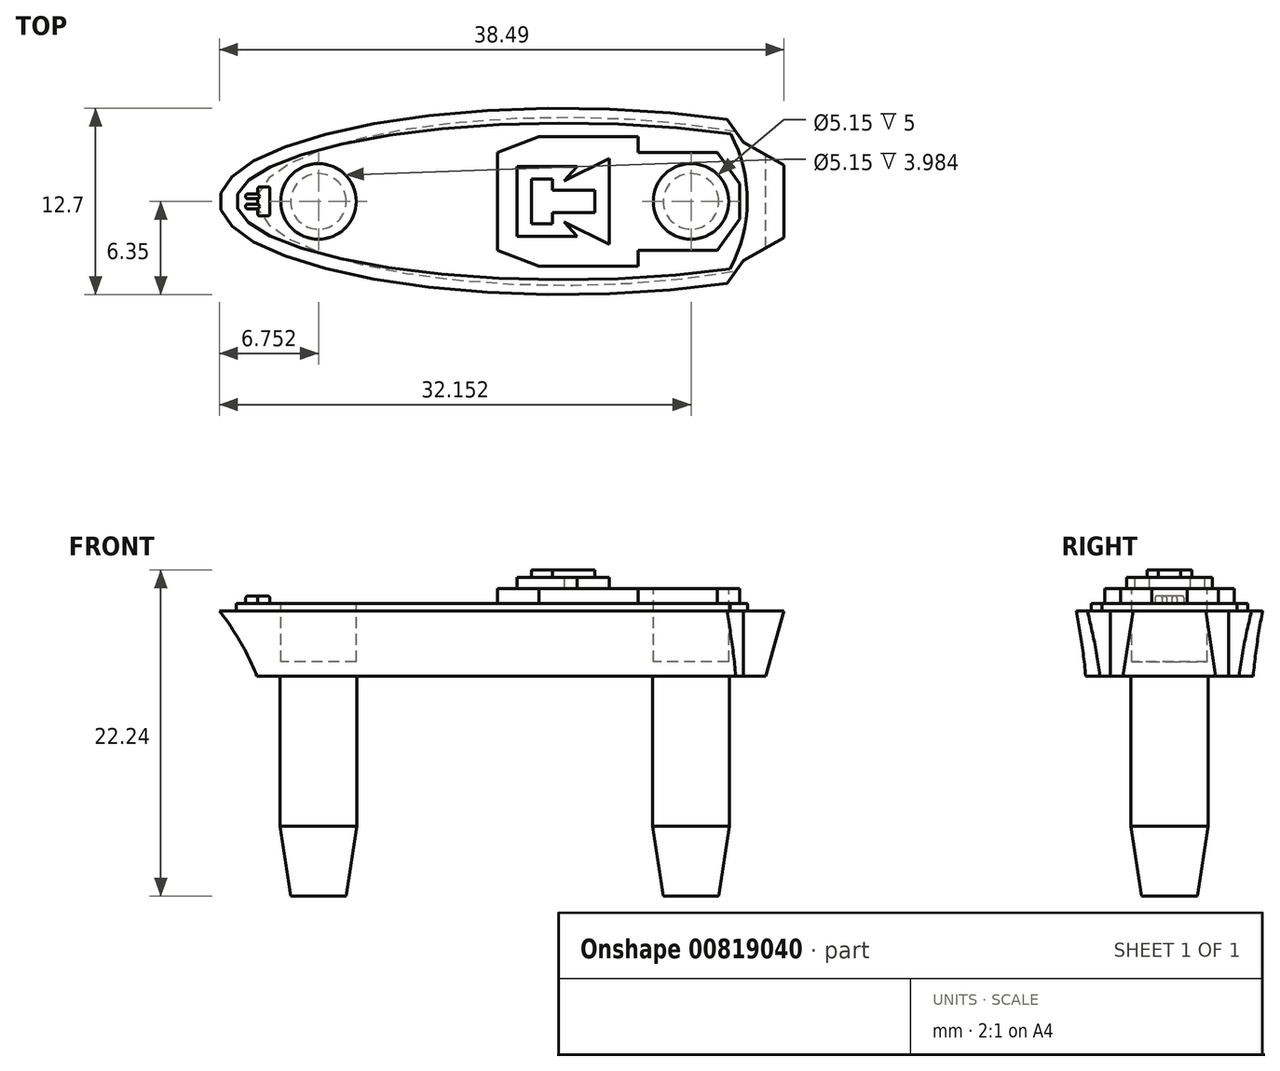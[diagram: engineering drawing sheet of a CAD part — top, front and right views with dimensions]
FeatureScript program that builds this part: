
annotation { "Feature Type Name" : "Feature", "Feature Type Description" : "" }
export const myFeature = defineFeature(function(context is Context, id is Id, definition is map)
    precondition{}
    {
        {
            var Q0;
            Q0=qCreatedBy(makeId("Top.planeOp"),FACE);
            var sketch = newSketch(context, id + "F0", { "sketchPlane" : qUnion([Q0])});
            skEllipse(sketch, "E0", {"center": v(0, 0) * mm, "majorRadius": 20.96 * mm, "minorRadius": 5.72 * mm, "majorAxis": v(1, 0)});
            skSolve(sketch);
        }
        {
            var Q0;
            Q0=qCreatedBy(makeId("Top.planeOp"),FACE);
            cPlane(context, id + "F1", {"entities" : qUnion([Q0]), "cplaneType" : CPlaneType.OFFSET, "offset" : 4.44 * mm, "width" : 152.4 * mm, "height" : 152.4 * mm});
        }
        {
            var Q0;
            Q0=qCreatedBy(id+"F1.planeOp",FACE);
            var sketch = newSketch(context, id + "F2", { "sketchPlane" : qUnion([Q0])});
            skEllipse(sketch, "E1", {"center": v(0, 0) * mm, "majorRadius": 23.5 * mm, "minorRadius": 6.35 * mm, "majorAxis": v(1, 0)});
            skPoint(sketch, "E2", {"position": v(23.5, 0) * mm});
            skSolve(sketch);
        }
        {
            var Q0;
            Q0=makeQuery(id+"F0.imprint","IMPRINT",FACE,{"disambiguationData":[TD([[makeQuery(id+"F0.imprint","IMPRINT",EDGE,{"derivedFrom":sQuery(id+"F0.wireOp",EDGE,"E0")}),1.0]])]});
            var Q1;
            Q1=makeQuery(id+"F2.imprint","IMPRINT",FACE,{"disambiguationData":[TD([[makeQuery(id+"F2.imprint","IMPRINT",EDGE,{"derivedFrom":sQuery(id+"F2.wireOp",EDGE,"E1")}),1.0]])]});
            loft(context, id + "F3", {"sheetProfilesArray" : [{ "sheetProfileEntities" : qUnion([Q0]) }, { "sheetProfileEntities" : qUnion([Q1]) }]});
        }
        {
            var Q0;
            Q0=qCreatedBy(makeId("Front.planeOp"),FACE);
            var sketch = newSketch(context, id + "F4", { "sketchPlane" : qUnion([Q0])});
            skLineSegment(sketch, "E3", {"start": v(12.95, -2.92) * mm, "end": v(15.07, 4.71) * mm});
            skPoint(sketch, "E4", {"position": v(14.6, 3.05) * mm});
            skPoint(sketch, "E5", {"position": v(13.76, 0) * mm});
            skPoint(sketch, "E6", {"position": v(-23.5, 3.05) * mm});
            skSolve(sketch);
        }
        {
            var Q0;
            Q0=sQuery(id+"F4.wireOp",EDGE,"E3");
            cPlane(context, id + "F5", {"entities" : qUnion([Q0]), "cplaneType" : CPlaneType.LINE_ANGLE, "offset" : 25.4 * mm, "angle" : 0 * degree, "width" : 152.4 * mm, "height" : 152.4 * mm});
        }
        {
            var Q0;
            Q0=qCreatedBy(id+"F5.planeOp",FACE);
            var sketch = newSketch(context, id + "F6", { "sketchPlane" : qUnion([Q0])});
            skLineSegment(sketch, "E7.bottom", {"start": v(-4.95, 12.51) * mm, "end": v(5, 12.51) * mm});
            skLineSegment(sketch, "E7.top", {"start": v(-4.95, 0.69) * mm, "end": v(5, 0.69) * mm});
            skLineSegment(sketch, "E7.left", {"start": v(-4.95, 12.51) * mm, "end": v(-4.95, 0.69) * mm});
            skLineSegment(sketch, "E7.right", {"start": v(5, 12.51) * mm, "end": v(5, 0.69) * mm});
            skSolve(sketch);
        }
        {
            var Q0;
            Q0=makeQuery(id+"F6.imprint","IMPRINT",FACE,{"disambiguationData":[TD([[makeQuery(id+"F6.imprint","IMPRINT",EDGE,{"derivedFrom":sQuery(id+"F6.wireOp",EDGE,"E7.bottom")}),-1.0]])]});
            extrude(context, id + "F7", {"entities" : qUnion([Q0]), "operationType" : NewBodyOperationType.REMOVE, "oppositeDirection" : true, "depth" : -76.2 * mm, "offsetDistance" : 25.4 * mm});
        }
        {
            var Q0;
            Q0=makeQuery(id+"F3.opLoft","CAP_FACE",FACE,{"disambiguationData":[OSD([makeQuery(id+"F2.imprint","IMPRINT",FACE,{"disambiguationData":[TD([[makeQuery(id+"F2.imprint","IMPRINT",EDGE,{"derivedFrom":sQuery(id+"F2.wireOp",EDGE,"E1")}),1.0]])]})])],"isStart":true});
            var sketch = newSketch(context, id + "F8", { "sketchPlane" : qUnion([Q0])});
            skLineSegment(sketch, "E8", {"start": v(-24.83, 0) * mm, "end": v(22.16, 0) * mm, "construction": true});
            skLineSegment(sketch, "E9", {"start": v(11.1, -5.6) * mm, "end": v(12.2, -4.02) * mm});
            skLineSegment(sketch, "E10", {"start": v(12.2, -4.02) * mm, "end": v(15, -2.47) * mm});
            skLineSegment(sketch, "E11", {"start": v(11.1, -5.6) * mm, "end": v(12.84, -9.26) * mm});
            skLineSegment(sketch, "E12", {"start": v(12.84, -9.26) * mm, "end": v(16.72, -4.38) * mm});
            skLineSegment(sketch, "E13", {"start": v(16.72, -4.38) * mm, "end": v(15, -2.47) * mm});
            skLineSegment(sketch, "E14.MirrorCS", {"start": v(11.1, 5.6) * mm, "end": v(12.2, 4.02) * mm});
            skLineSegment(sketch, "E15.MirrorCS", {"start": v(12.2, 4.02) * mm, "end": v(15, 2.47) * mm});
            skLineSegment(sketch, "E16.MirrorCS", {"start": v(11.1, 5.6) * mm, "end": v(12.84, 9.26) * mm});
            skLineSegment(sketch, "E17.MirrorCS", {"start": v(12.84, 9.26) * mm, "end": v(16.72, 4.38) * mm});
            skLineSegment(sketch, "E18.MirrorCS", {"start": v(16.72, 4.38) * mm, "end": v(15, 2.47) * mm});
            skSolve(sketch);
        }
        {
            var Q0;
            {var subQ0=sQuery(id+"F8.wireOp",EDGE,"E9");Q0=makeQuery(id+"F8.imprint","IMPRINT",FACE,{"disambiguationData":[TD([[makeQuery(id+"F8.imprint","IMPRINT",EDGE,{"derivedFrom":subQ0}),-1.0]])]});}
            var Q1;
            {var subQ0=sQuery(id+"F8.wireOp",EDGE,"E14.MirrorCS");Q1=makeQuery(id+"F8.imprint","IMPRINT",FACE,{"disambiguationData":[TD([[makeQuery(id+"F8.imprint","IMPRINT",EDGE,{"derivedFrom":subQ0}),1.0]])]});}
            extrude(context, id + "F9", {"entities" : qUnion([Q0, Q1]), "operationType" : NewBodyOperationType.REMOVE, "endBound" : BoundingType.THROUGH_ALL, "oppositeDirection" : true, "depth" : 25.4 * mm, "offsetDistance" : 25.4 * mm});
        }
        {
            var Q0;
            Q0=makeQuery(id+"F3.opLoft","CAP_FACE",FACE,{"disambiguationData":[OSD([makeQuery(id+"F2.imprint","IMPRINT",FACE,{"disambiguationData":[TD([[makeQuery(id+"F2.imprint","IMPRINT",EDGE,{"derivedFrom":sQuery(id+"F2.wireOp",EDGE,"E1")}),1.0]])]})])],"isStart":true});
            var sketch = newSketch(context, id + "F10", { "sketchPlane" : qUnion([Q0])});
            skEllipticalArc(sketch, "E19", {});
            skArc(sketch, "E20", {"start": v(11.31, -4.6) * mm, "mid": v(12.5, 0) * mm, "end": v(11.36, 4.6) * mm});
            skLineSegment(sketch, "E21", {"start": v(0, 0) * mm, "end": v(2.75, 0.04) * mm, "construction": true});
            const initialGuessF10  = {"E19": [0, 0, -1, 0, 0.022352, 0.005334, 4.179158944691912, 2.101455414401311]};
            skSetInitialGuess(sketch, initialGuessF10);
            skSolve(sketch);
        }
        {
            var Q0;
            Q0=makeQuery(id+"F10.imprint","IMPRINT",FACE,{"disambiguationData":[TD([[makeQuery(id+"F10.imprint","IMPRINT",EDGE,{"derivedFrom":sQuery(id+"F10.wireOp",EDGE,"E19")}),1.0]])]});
            extrude(context, id + "F11", {"entities" : qUnion([Q0]), "operationType" : NewBodyOperationType.ADD, "depth" : 0.5 * mm, "offsetDistance" : 25.4 * mm});
        }
        {
            var Q0;
            Q0=makeQuery(id+"F11.opExtrude","CAP_FACE",FACE,{"disambiguationData":[OSD([sQuery(id+"F10.wireOp",EDGE,"E19"),sQuery(id+"F10.wireOp",EDGE,"E20")])],"isStart":false});
            var sketch = newSketch(context, id + "F12", { "sketchPlane" : qUnion([Q0])});
            skLineSegment(sketch, "E22.left", {"start": v(11.95, -1.2) * mm, "end": v(11.95, 1.2) * mm});
            skLineSegment(sketch, "E23.top", {"start": v(5.04, 4.42) * mm, "end": v(-1.7, 4.42) * mm});
            skLineSegment(sketch, "E23.left", {"start": v(5.04, -4.42) * mm, "end": v(5.04, -3.33) * mm});
            skLineSegment(sketch, "E23.right", {"start": v(-4.55, -4.42) * mm, "end": v(-4.55, -4.42) * mm});
            skLineSegment(sketch, "E24.trimOffspring", {"start": v(5.04, 3.33) * mm, "end": v(5.04, 4.42) * mm});
            skLineSegment(sketch, "E25", {"start": v(-9.84, 0) * mm, "end": v(11.02, 0) * mm, "construction": true});
            skLineSegment(sketch, "E26", {"start": v(-4.55, 3.33) * mm, "end": v(-1.7, 4.42) * mm});
            skLineSegment(sketch, "E27.MirrorCS", {"start": v(10.44, 3.33) * mm, "end": v(5.04, 3.33) * mm});
            skLineSegment(sketch, "E28", {"start": v(10.44, 3.33) * mm, "end": v(11.95, 1.2) * mm});
            skPoint(sketch, "E29.orphan", {"position": v(-4.55, 4.42) * mm});
            skLineSegment(sketch, "E30.trimOffspring", {"start": v(11.95, 3.33) * mm, "end": v(11.95, 3.33) * mm});
            skPoint(sketch, "E31.MirrorCS.start.orphan", {"position": v(5.04, 4.42) * mm});
            skPoint(sketch, "E32.MirrorCS.end.orphan", {"position": v(-4.55, -4.42) * mm});
            skPoint(sketch, "E32.MirrorCS.start.orphan", {"position": v(5.04, -4.42) * mm});
            skPoint(sketch, "E33.MirrorCS.end.orphan", {"position": v(5.04, -3.33) * mm});
            skPoint(sketch, "E33.MirrorCS.start.orphan", {"position": v(11.95, -3.33) * mm});
            skLineSegment(sketch, "E34.MirrorCS", {"start": v(-4.55, -3.33) * mm, "end": v(-1.7, -4.42) * mm});
            skLineSegment(sketch, "E35.MirrorCS", {"start": v(10.44, -3.33) * mm, "end": v(11.95, -1.2) * mm});
            skLineSegment(sketch, "E36.MirrorCS", {"start": v(10.44, -3.33) * mm, "end": v(5.04, -3.33) * mm});
            skLineSegment(sketch, "E37.MirrorCS", {"start": v(5.04, -4.42) * mm, "end": v(-1.7, -4.42) * mm});
            skLineSegment(sketch, "E38.trimOffspring", {"start": v(-4.55, -3.33) * mm, "end": v(-4.55, 3.33) * mm});
            skSolve(sketch);
        }
        {
            var Q0;
            Q0=makeQuery(id+"F12.imprint","IMPRINT",FACE,{"disambiguationData":[TD([[makeQuery(id+"F12.imprint","IMPRINT",EDGE,{"derivedFrom":sQuery(id+"F12.wireOp",EDGE,"E22.left")}),1.0]])]});
            extrude(context, id + "F13", {"entities" : qUnion([Q0]), "operationType" : NewBodyOperationType.ADD, "depth" : 1.02 * mm, "offsetDistance" : 25.4 * mm});
        }
        {
            var Q0;
            Q0=makeQuery(id+"F13.opExtrude","CAP_FACE",FACE,{"disambiguationData":[OSD([sQuery(id+"F12.wireOp",EDGE,"E22.left"),sQuery(id+"F12.wireOp",EDGE,"E23.top"),sQuery(id+"F12.wireOp",EDGE,"E23.left"),sQuery(id+"F12.wireOp",EDGE,"E24.trimOffspring"),sQuery(id+"F12.wireOp",EDGE,"E26"),sQuery(id+"F12.wireOp",EDGE,"E27.MirrorCS"),sQuery(id+"F12.wireOp",EDGE,"E28"),sQuery(id+"F12.wireOp",EDGE,"E34.MirrorCS"),sQuery(id+"F12.wireOp",EDGE,"E35.MirrorCS"),sQuery(id+"F12.wireOp",EDGE,"E36.MirrorCS"),sQuery(id+"F12.wireOp",EDGE,"E37.MirrorCS"),sQuery(id+"F12.wireOp",EDGE,"E38.trimOffspring")])],"isStart":false});
            var sketch = newSketch(context, id + "F14", { "sketchPlane" : qUnion([Q0])});
            skLineSegment(sketch, "E39", {"start": v(-16.75, 0) * mm, "end": v(8.65, 0) * mm, "construction": true});
            skCircle(sketch, "E40", {"center": v(-16.75, 0) * mm, "radius": 2.58 * mm});
            skCircle(sketch, "E41", {"center": v(8.65, 0) * mm, "radius": 2.58 * mm});
            skSolve(sketch);
        }
        {
            var Q0;
            Q0=makeQuery(id+"F14.imprint","IMPRINT",FACE,{"disambiguationData":[TD([[makeQuery(id+"F14.imprint","IMPRINT",EDGE,{"derivedFrom":sQuery(id+"F14.wireOp",EDGE,"E41")}),-1.0]])]});
            var sketch = newSketch(context, id + "F15", { "sketchPlane" : qUnion([Q0])});
            skLineSegment(sketch, "E42", {"start": v(3.08, -2.93) * mm, "end": v(3.08, 2.93) * mm});
            skLineSegment(sketch, "E43", {"start": v(3.08, 2.93) * mm, "end": v(0, 1.4) * mm});
            skLineSegment(sketch, "E44", {"start": v(0, -1.4) * mm, "end": v(3.08, -2.93) * mm});
            skLineSegment(sketch, "E45", {"start": v(0, -1.4) * mm, "end": v(0.9, -2.38) * mm});
            skLineSegment(sketch, "E46", {"start": v(0.9, -2.38) * mm, "end": v(-3.2, -2.38) * mm});
            skLineSegment(sketch, "E47", {"start": v(-3.2, -2.38) * mm, "end": v(-3.2, 2.38) * mm});
            skLineSegment(sketch, "E48", {"start": v(-3.2, 2.38) * mm, "end": v(0.9, 2.38) * mm});
            skLineSegment(sketch, "E49", {"start": v(0.9, 2.38) * mm, "end": v(0, 1.4) * mm});
            skLineSegment(sketch, "E50", {"start": v(-3.65, 0) * mm, "end": v(-4.7, 0) * mm, "construction": true});
            skPoint(sketch, "E51.orphan", {"position": v(-2.78, 0) * mm});
            skSolve(sketch);
        }
        {
            var Q0;
            Q0=makeQuery(id+"F15.imprint","IMPRINT",FACE,{"disambiguationData":[TD([[makeQuery(id+"F15.imprint","IMPRINT",EDGE,{"derivedFrom":sQuery(id+"F15.wireOp",EDGE,"E42")}),1.0]])]});
            extrude(context, id + "F16", {"entities" : qUnion([Q0]), "operationType" : NewBodyOperationType.ADD, "depth" : 0.76 * mm, "offsetDistance" : 25.4 * mm});
        }
        {
            var Q0;
            Q0=makeQuery(id+"F16.opExtrude","CAP_FACE",FACE,{"disambiguationData":[OSD([sQuery(id+"F15.wireOp",EDGE,"E42"),sQuery(id+"F15.wireOp",EDGE,"E43"),sQuery(id+"F15.wireOp",EDGE,"E44"),sQuery(id+"F15.wireOp",EDGE,"E45"),sQuery(id+"F15.wireOp",EDGE,"E46"),sQuery(id+"F15.wireOp",EDGE,"E47"),sQuery(id+"F15.wireOp",EDGE,"E48"),sQuery(id+"F15.wireOp",EDGE,"E49")])],"isStart":false});
            var sketch = newSketch(context, id + "F17", { "sketchPlane" : qUnion([Q0])});
            skLineSegment(sketch, "E52.bottom", {"start": v(-2.23, 1.53) * mm, "end": v(-0.8, 1.53) * mm});
            skLineSegment(sketch, "E52.top", {"start": v(-2.23, -1.53) * mm, "end": v(-0.8, -1.53) * mm});
            skLineSegment(sketch, "E52.left", {"start": v(-2.23, 1.53) * mm, "end": v(-2.23, -1.53) * mm});
            skLineSegment(sketch, "E52.right", {"start": v(-0.8, 1.53) * mm, "end": v(-0.8, 0.75) * mm});
            skLineSegment(sketch, "E53.bottom", {"start": v(-0.8, 0.75) * mm, "end": v(2.08, 0.75) * mm});
            skLineSegment(sketch, "E53.top", {"start": v(-0.8, -0.75) * mm, "end": v(2.08, -0.75) * mm});
            skLineSegment(sketch, "E53.right", {"start": v(2.08, 0.75) * mm, "end": v(2.08, -0.75) * mm});
            skLineSegment(sketch, "E54.trimOffspring", {"start": v(-0.8, -0.75) * mm, "end": v(-0.8, -1.53) * mm});
            skLineSegment(sketch, "E55", {"start": v(-6.5, 0) * mm, "end": v(-7.44, 0) * mm, "construction": true});
            skSolve(sketch);
        }
        {
            var Q0;
            Q0=makeQuery(id+"F17.imprint","IMPRINT",FACE,{"disambiguationData":[TD([[makeQuery(id+"F17.imprint","IMPRINT",EDGE,{"derivedFrom":sQuery(id+"F17.wireOp",EDGE,"E52.bottom")}),-1.0]])]});
            extrude(context, id + "F18", {"entities" : qUnion([Q0]), "operationType" : NewBodyOperationType.ADD, "depth" : 0.5 * mm, "offsetDistance" : 25.4 * mm});
        }
        {
            var Q0;
            Q0=makeQuery(id+"F3.opLoft","CAP_FACE",FACE,{"disambiguationData":[OSD([makeQuery(id+"F2.imprint","IMPRINT",FACE,{"disambiguationData":[TD([[makeQuery(id+"F2.imprint","IMPRINT",EDGE,{"derivedFrom":sQuery(id+"F2.wireOp",EDGE,"E1")}),1.0]])]})])],"isStart":true});
            var sketch = newSketch(context, id + "F19", { "sketchPlane" : qUnion([Q0])});
            skLineSegment(sketch, "E56.bottom", {"start": v(-20.19, 1) * mm, "end": v(-20.76, 1) * mm});
            skLineSegment(sketch, "E56.top", {"start": v(-20.19, -1) * mm, "end": v(-20.76, -1) * mm});
            skLineSegment(sketch, "E56.left", {"start": v(-20.06, 0.86) * mm, "end": v(-20.06, -0.86) * mm});
            skLineSegment(sketch, "E56.right", {"start": v(-20.88, 0.86) * mm, "end": v(-20.88, 0.5) * mm});
            skLineSegment(sketch, "E57", {"start": v(-17.48, 0) * mm, "end": v(-18.1, 0) * mm, "construction": true});
            skLineSegment(sketch, "E58.bottom", {"start": v(-20.88, 0.5) * mm, "end": v(-21.7, 0.5) * mm});
            skLineSegment(sketch, "E58.top", {"start": v(-20.88, 0.18) * mm, "end": v(-21.7, 0.18) * mm});
            skLineSegment(sketch, "E58.right", {"start": v(-21.7, 0.5) * mm, "end": v(-21.7, 0.18) * mm});
            skLineSegment(sketch, "E59.MirrorCS", {"start": v(-20.88, -0.18) * mm, "end": v(-21.7, -0.18) * mm});
            skLineSegment(sketch, "E60.MirrorCS", {"start": v(-20.88, -0.5) * mm, "end": v(-21.7, -0.5) * mm});
            skLineSegment(sketch, "E61.MirrorCS", {"start": v(-21.7, -0.5) * mm, "end": v(-21.7, -0.18) * mm});
            skLineSegment(sketch, "E62.trimOffspring", {"start": v(-20.88, 0.18) * mm, "end": v(-20.88, -0.18) * mm});
            skLineSegment(sketch, "E63.trimOffspring", {"start": v(-20.88, -0.5) * mm, "end": v(-20.88, -0.86) * mm});
            skArc(sketch, "E64.filletArc", {"start": v(-18.55, 2.93) * mm, "mid": v(-18.64, 2.9) * mm, "end": v(-18.67, 2.8) * mm, "construction": true});
            skPoint(sketch, "E65.visualSharp", {"position": v(-20.88, 1) * mm});
            skArc(sketch, "E65.filletArc", {"start": v(-20.76, 1) * mm, "mid": v(-20.84, 0.95) * mm, "end": v(-20.88, 0.86) * mm});
            skPoint(sketch, "E66.visualSharp", {"position": v(-20.06, 1) * mm});
            skArc(sketch, "E66.filletArc", {"start": v(-20.06, 0.86) * mm, "mid": v(-20.1, 0.95) * mm, "end": v(-20.19, 1) * mm});
            skPoint(sketch, "E67.visualSharp", {"position": v(-20.06, -1) * mm});
            skArc(sketch, "E67.filletArc", {"start": v(-20.19, -1) * mm, "mid": v(-20.1, -0.95) * mm, "end": v(-20.06, -0.86) * mm});
            skPoint(sketch, "E68.visualSharp", {"position": v(-20.88, -1) * mm});
            skArc(sketch, "E68.filletArc", {"start": v(-20.88, -0.86) * mm, "mid": v(-20.84, -0.95) * mm, "end": v(-20.76, -1) * mm});
            skSolve(sketch);
        }
        {
            var Q0;
            Q0=makeQuery(id+"F19.imprint","IMPRINT",FACE,{"disambiguationData":[TD([[makeQuery(id+"F19.imprint","IMPRINT",EDGE,{"derivedFrom":sQuery(id+"F19.wireOp",EDGE,"E56.bottom")}),1.0]])]});
            extrude(context, id + "F20", {"entities" : qUnion([Q0]), "operationType" : NewBodyOperationType.ADD, "depth" : 0.5 * mm, "offsetDistance" : 25.4 * mm});
        }
        {
            var Q0;
            Q0=makeQuery(id+"F14.imprint","IMPRINT",FACE,{"disambiguationData":[TD([[makeQuery(id+"F14.imprint","IMPRINT",EDGE,{"derivedFrom":sQuery(id+"F14.wireOp",EDGE,"E40")}),1.0]])]});
            var Q1;
            Q1=makeQuery(id+"F14.imprint","IMPRINT",FACE,{"disambiguationData":[TD([[makeQuery(id+"F14.imprint","IMPRINT",EDGE,{"derivedFrom":sQuery(id+"F14.wireOp",EDGE,"E41")}),1.0]])]});
            extrude(context, id + "F21", {"entities" : qUnion([Q0, Q1]), "operationType" : NewBodyOperationType.REMOVE, "oppositeDirection" : true, "depth" : 5 * mm, "offsetDistance" : 25.4 * mm});
        }
        {
            var Q0;
            Q0=makeQuery(id+"F3.opLoft","CAP_FACE",FACE,{"disambiguationData":[OSD([makeQuery(id+"F0.imprint","IMPRINT",FACE,{"disambiguationData":[TD([[makeQuery(id+"F0.imprint","IMPRINT",EDGE,{"derivedFrom":sQuery(id+"F0.wireOp",EDGE,"E0")}),1.0]])]})])],"isStart":true});
            var sketch = newSketch(context, id + "F22", { "sketchPlane" : qUnion([Q0])});
            skLineSegment(sketch, "E69", {"start": v(-16.75, 0) * mm, "end": v(8.65, 0) * mm, "construction": true});
            skCircle(sketch, "E70", {"center": v(-16.75, 0) * mm, "radius": 2.62 * mm});
            skCircle(sketch, "E71", {"center": v(8.65, 0) * mm, "radius": 2.62 * mm});
            skSolve(sketch);
        }
        {
            var Q0;
            Q0=makeQuery(id+"F22.imprint","IMPRINT",FACE,{"disambiguationData":[TD([[makeQuery(id+"F22.imprint","IMPRINT",EDGE,{"derivedFrom":sQuery(id+"F22.wireOp",EDGE,"E70")}),1.0]])]});
            var Q1;
            Q1=makeQuery(id+"F22.imprint","IMPRINT",FACE,{"disambiguationData":[TD([[makeQuery(id+"F22.imprint","IMPRINT",EDGE,{"derivedFrom":sQuery(id+"F22.wireOp",EDGE,"E71")}),1.0]])]});
            extrude(context, id + "F23", {"entities" : qUnion([Q0, Q1]), "operationType" : NewBodyOperationType.ADD, "depth" : 15 * mm, "offsetDistance" : 25.4 * mm});
        }
        {
            var Q0;
            Q0=makeQuery(id+"F23.opExtrude","CAP_EDGE",EDGE,{"disambiguationData":[OSD([sQuery(id+"F22.wireOp",EDGE,"E71")])],"isStart":false});
            var Q1;
            Q1=makeQuery(id+"F23.opExtrude","CAP_EDGE",EDGE,{"disambiguationData":[OSD([sQuery(id+"F22.wireOp",EDGE,"E70")])],"isStart":false});
            chamfer(context, id + "F24", {"entities" : qUnion([Q0, Q1]), "chamferType" : ChamferType.TWO_OFFSETS, "width1" : 0.73 * mm, "oppositeDirection" : false, "width2" : 4.76 * mm, "tangentPropagation" : true});
        }
        {
            var Q0;
            Q0 = qSketchRegion(id + "F19", true);
            extrude(context, id + "F25", {"entities" : qUnion([Q0]), "operationType" : NewBodyOperationType.ADD, "depth" : 1 * mm, "offsetDistance" : 25.4 * mm});
        }
        {
            var Q0;
            Q0=makeQuery(id+"F25.opExtrude","CAP_EDGE",EDGE,{"disambiguationData":[OSD([sQuery(id+"F19.wireOp",EDGE,"E56.left")])],"isStart":false});
            var Q1;
            Q1=makeQuery(id+"F25.opExtrude","CAP_EDGE",EDGE,{"disambiguationData":[OSD([sQuery(id+"F19.wireOp",EDGE,"E60.MirrorCS")])],"isStart":false});
            var Q2;
            Q2=makeQuery(id+"F25.opExtrude","CAP_EDGE",EDGE,{"disambiguationData":[OSD([sQuery(id+"F19.wireOp",EDGE,"E58.top")])],"isStart":false});
            var Q3;
            Q3=makeQuery(id+"F25.opExtrude","CAP_EDGE",EDGE,{"disambiguationData":[OSD([sQuery(id+"F19.wireOp",EDGE,"E58.bottom")])],"isStart":false});
            var Q4;
            Q4=makeQuery(id+"F25.opExtrude","CAP_EDGE",EDGE,{"disambiguationData":[OSD([sQuery(id+"F19.wireOp",EDGE,"E62.trimOffspring")])],"isStart":false});
            var Q5;
            Q5=makeQuery(id+"F25.opExtrude","CAP_EDGE",EDGE,{"disambiguationData":[OSD([sQuery(id+"F19.wireOp",EDGE,"E59.MirrorCS")])],"isStart":false});
            var Q6;
            Q6=makeQuery(id+"F25.opExtrude","CAP_EDGE",EDGE,{"disambiguationData":[OSD([sQuery(id+"F19.wireOp",EDGE,"E61.MirrorCS")])],"isStart":false});
            var Q7;
            Q7=makeQuery(id+"F25.opExtrude","CAP_EDGE",EDGE,{"disambiguationData":[OSD([sQuery(id+"F19.wireOp",EDGE,"E58.right")])],"isStart":false});
            var Q8;
            Q8=makeQuery(id+"F25.opExtrude","SWEPT_EDGE",EDGE,{"disambiguationData":[OSD([sQuery(id+"F19.wireOp",EDGE,"E60.MirrorCS"),sQuery(id+"F19.wireOp",EDGE,"E61.MirrorCS")])]});
            var Q9;
            Q9=makeQuery(id+"F25.opExtrude","SWEPT_EDGE",EDGE,{"disambiguationData":[OSD([sQuery(id+"F19.wireOp",EDGE,"E59.MirrorCS"),sQuery(id+"F19.wireOp",EDGE,"E61.MirrorCS")])]});
            var Q10;
            Q10=makeQuery(id+"F25.opExtrude","SWEPT_EDGE",EDGE,{"disambiguationData":[OSD([sQuery(id+"F19.wireOp",EDGE,"E58.top"),sQuery(id+"F19.wireOp",EDGE,"E58.right")])]});
            var Q11;
            Q11=makeQuery(id+"F25.opExtrude","SWEPT_EDGE",EDGE,{"disambiguationData":[OSD([sQuery(id+"F19.wireOp",EDGE,"E58.bottom"),sQuery(id+"F19.wireOp",EDGE,"E58.right")])]});
            fillet(context, id + "F26", {"entities" : qUnion([Q0, Q1, Q2, Q3, Q4, Q5, Q6, Q7, Q8, Q9, Q10, Q11]), "tangentPropagation" : true, "radius" : 0.13 * mm, "defaultsChanged" : false, "vertexSettings" : [], "allowEdgeOverflow" : false});
        }
    });
